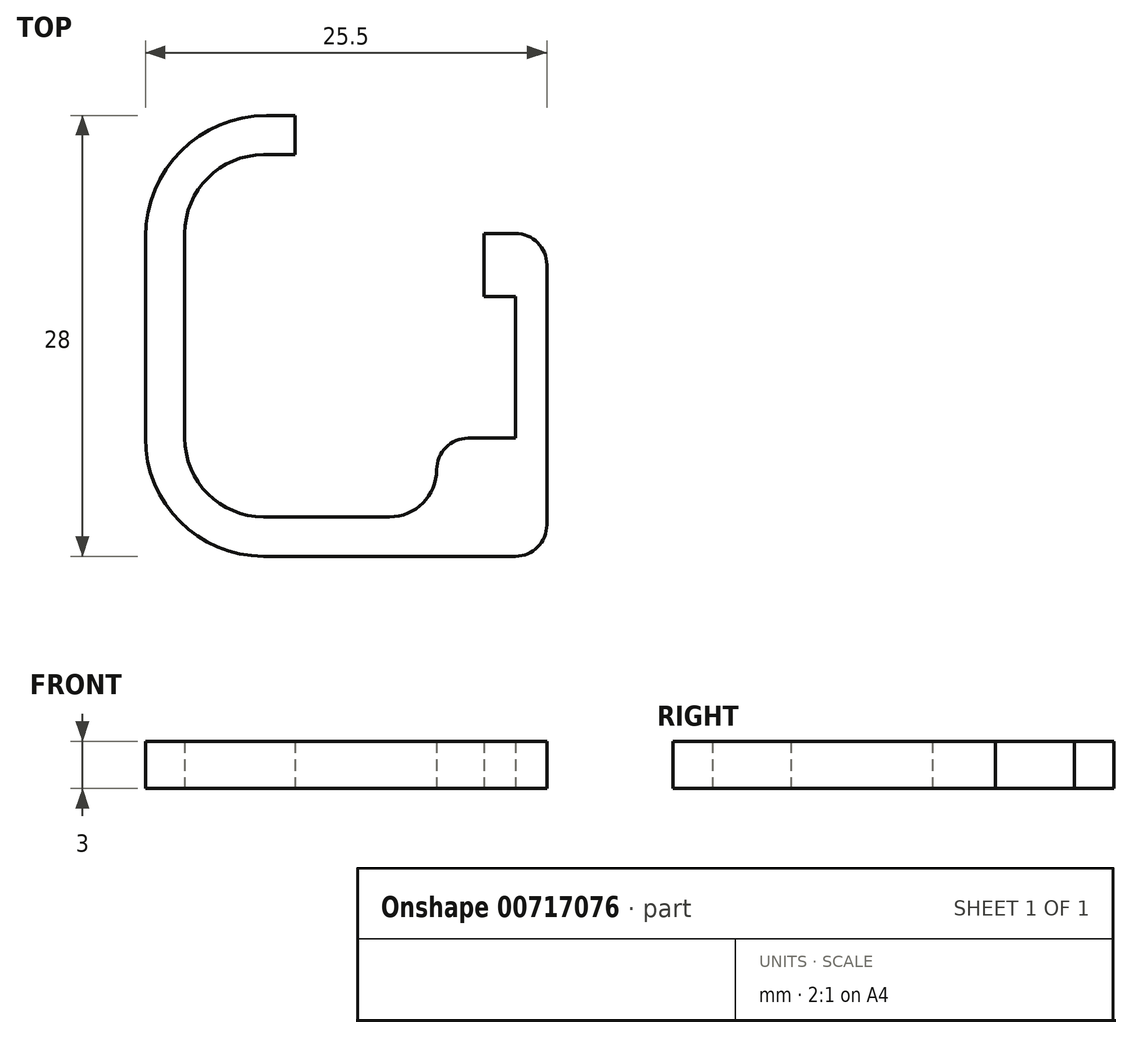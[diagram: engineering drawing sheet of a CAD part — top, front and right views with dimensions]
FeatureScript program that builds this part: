
annotation { "Feature Type Name" : "Feature", "Feature Type Description" : "" }
export const myFeature = defineFeature(function(context is Context, id is Id, definition is map)
    precondition{}
    {
        {
            var Q0;
            Q0=qCreatedBy(makeId("Top.planeOp"),FACE);
            var sketch = newSketch(context, id + "F0", { "sketchPlane" : qUnion([Q0])});
            skLineSegment(sketch, "E0", {"start": v(0, 0) * mm, "end": v(0, -20.5) * mm});
            skLineSegment(sketch, "E1", {"start": v(0, -20.5) * mm, "end": v(-18, -20.5) * mm});
            skLineSegment(sketch, "E2", {"start": v(-25.5, -13) * mm, "end": v(-25.5, -0.2) * mm});
            skLineSegment(sketch, "E3", {"start": v(0, 0) * mm, "end": v(-4, 0) * mm});
            skLineSegment(sketch, "E4", {"start": v(-4, 0) * mm, "end": v(-4, -4) * mm});
            skLineSegment(sketch, "E5", {"start": v(-4, -4) * mm, "end": v(-2, -4) * mm});
            skLineSegment(sketch, "E6", {"start": v(-10, -18) * mm, "end": v(-18, -18) * mm});
            skLineSegment(sketch, "E7", {"start": v(-23, -13) * mm, "end": v(-23, 0) * mm});
            skLineSegment(sketch, "E8", {"start": v(-18, 5) * mm, "end": v(-16, 5) * mm});
            skLineSegment(sketch, "E9", {"start": v(-16, 5) * mm, "end": v(-16, 7.5) * mm});
            skLineSegment(sketch, "E10", {"start": v(-16, 7.5) * mm, "end": v(-17.8, 7.5) * mm});
            skLineSegment(sketch, "E11", {"start": v(-7, -15) * mm, "end": v(-7, -15) * mm});
            skLineSegment(sketch, "E12", {"start": v(-5, -13) * mm, "end": v(-2, -13) * mm});
            skLineSegment(sketch, "E13", {"start": v(-2, -13) * mm, "end": v(-2, -4) * mm});
            skPoint(sketch, "E14.visualSharp", {"position": v(-23, 5) * mm});
            skArc(sketch, "E14.filletArc", {"start": v(-18, 5) * mm, "mid": v(-21.54, 3.54) * mm, "end": v(-23, 0) * mm});
            skPoint(sketch, "E15.visualSharp", {"position": v(-23, -18) * mm});
            skArc(sketch, "E15.filletArc", {"start": v(-23, -13) * mm, "mid": v(-21.54, -16.54) * mm, "end": v(-18, -18) * mm});
            skPoint(sketch, "E16.visualSharp", {"position": v(-7, -18) * mm});
            skArc(sketch, "E16.filletArc", {"start": v(-10, -18) * mm, "mid": v(-7.88, -17.12) * mm, "end": v(-7, -15) * mm});
            skPoint(sketch, "E17.visualSharp", {"position": v(-7, -13) * mm});
            skArc(sketch, "E17.filletArc", {"start": v(-5, -13) * mm, "mid": v(-6.41, -13.59) * mm, "end": v(-7, -15) * mm});
            skPoint(sketch, "E18.visualSharp", {"position": v(-25.5, -20.5) * mm});
            skArc(sketch, "E18.filletArc", {"start": v(-25.5, -13) * mm, "mid": v(-23.3, -18.3) * mm, "end": v(-18, -20.5) * mm});
            skPoint(sketch, "E19.visualSharp", {"position": v(-25.5, 7.5) * mm});
            skArc(sketch, "E19.filletArc", {"start": v(-17.8, 7.5) * mm, "mid": v(-23.24, 5.24) * mm, "end": v(-25.5, -0.2) * mm});
            skSolve(sketch);
        }
        {
            var Q0;
            Q0=makeQuery(id+"F0.imprint","IMPRINT",FACE,{"disambiguationData":[TD([[makeQuery(id+"F0.imprint","IMPRINT",EDGE,{"derivedFrom":sQuery(id+"F0.wireOp",EDGE,"E0")}),-1.0]])]});
            extrude(context, id + "F1", {"entities" : qUnion([Q0]), "depth" : 3 * mm, "offsetDistance" : 25 * mm});
        }
        {
            var Q0;
            Q0=makeQuery(id+"F1.opExtrude","SWEPT_EDGE",EDGE,{"disambiguationData":[OSD([sQuery(id+"F0.wireOp",EDGE,"E2"),sQuery(id+"F0.wireOp",EDGE,"E18.filletArc")])]});
            var Q1;
            Q1=makeQuery(id+"F1.opExtrude","SWEPT_EDGE",EDGE,{"disambiguationData":[OSD([sQuery(id+"F0.wireOp",EDGE,"E2"),sQuery(id+"F0.wireOp",EDGE,"E19.filletArc")])]});
            var Q2;
            Q2=makeQuery(id+"F1.opExtrude","SWEPT_EDGE",EDGE,{"disambiguationData":[OSD([sQuery(id+"F0.wireOp",EDGE,"E0"),sQuery(id+"F0.wireOp",EDGE,"E3")])]});
            var Q3;
            Q3=makeQuery(id+"F1.opExtrude","SWEPT_EDGE",EDGE,{"disambiguationData":[OSD([sQuery(id+"F0.wireOp",EDGE,"E0"),sQuery(id+"F0.wireOp",EDGE,"E1")])]});
            var Q4;
            Q4=makeQuery(id+"F1.opExtrude","SWEPT_EDGE",EDGE,{"disambiguationData":[OSD([sQuery(id+"F0.wireOp",EDGE,"E1"),sQuery(id+"F0.wireOp",EDGE,"E18.filletArc")])]});
            fillet(context, id + "F2", {"entities" : qUnion([Q0, Q1, Q2, Q3, Q4]), "radius" : 2 * mm, "tangentPropagation" : true, "allowEdgeOverflow" : false});
        }
    });
